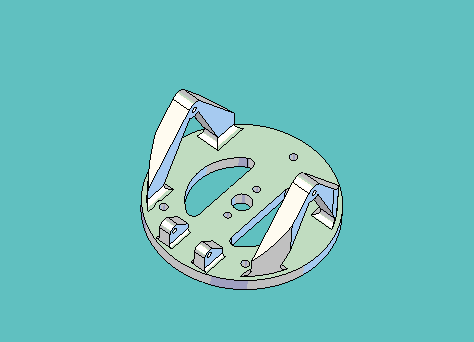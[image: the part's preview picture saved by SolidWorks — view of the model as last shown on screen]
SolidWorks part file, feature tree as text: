
SOLIDWORKS PART (.sldprt)
format: sldprt  version: not decoded by parser v0  size: 1,202,688 bytes
history: native  units: mm
features: sketch x15, cut_extrude x10, plane x7, extrude x5, fillet x3, material x1 (+11 scaffold rows collapsed)
feature tree (52):
  scaffold x11  (default folders/planes/origin — collapsed)
  material  "Material <not specified>"
  sketch  "Sketch1"  dims[c1.D1=50.8mm c1.D7=3.175mm c2.D1=89.1032mm c2.D2=~93.32036mm c3.D2=45.0deg c3.D3=~94.913632mm c4.D3=45.0deg c4.D4=6.35mm c4.D5=6.35mm c4.D6=31.75mm]
  extrude  "Extrude1"  Depth=6.35mm
  sketch  "Sketch2"  dims[c1.D1=50.8mm c1.D7=~3.96875mm c2.D1=~3.96875mm c2.D4=~3.96875mm c2.D6=69.85mm c2.D2=~93.32036mm c3.D2=163.0deg c3.D3=~94.913632mm c4.D3=45.0deg c4.D4=4.7625mm c4.D5=4.7625mm c4.D6=31.75mm c4.D1=4.7625mm c5.D6=34.925mm c5.D2=~82.034109mm c6.D2=30.0deg c6.D3=~82.034109mm c7.D3=107.0deg c7.D5=~82.034109mm c8.D5=167.0deg]
  cut_extrude  "Cut-Extrude8"  [1 undecoded]
  sketch  "Sketch3"  dims[c1.D1=3.4544mm c1.D2=3.4544mm c1.D3=9.525mm c1.D5=~19.84375mm c1.D4=~65.353861mm c2.D4=30.0deg]
  cut_extrude  "Cut-Extrude2"  [1 undecoded]
  sketch  "Sketch5"  dims[c1.D3=19.05mm c1.D4=25.4mm c1.D1=20.6375mm c1.D2=20.6375mm c1.D5=~49.79749mm c2.D5=30.0deg c2.D6=11.1125mm c2.D1=17.145mm c2.D2=17.145mm c3.D1=~82.457251mm c4.D1=90.0deg c4.D2=9.525mm c4.D3=9.525mm]
  cut_extrude  "Cut-Extrude4"  [1 undecoded]
  fillet  "Fillet2"  Radius=3.175mm
  sketch  "Sketch6"  dims[D1=9.525mm]
  extrude  "Axis2"  [1 undecoded]
  plane  "Plane1"
  plane  "Plane2"
  plane  "Plane3"  Offset=50.8mm
  sketch  "Sketch11"  dims[c1.D1=40.3225mm c1.D2=40.3225mm c2.D1=22.86mm c2.D2=24.384mm c2.D3=30.1625mm c2.D4=30.1625mm]
  extrude  "Extrude6"  Depth=44.45mm
  sketch  "Sketch7"  dims[D1=2.7051mm D2=4.7625mm]
  cut_extrude  "Cut-Extrude7"  [1 undecoded]
  sketch  "Sketch12"  dims[D1=6.35mm D2=6.35mm D3=6.35mm]
  cut_extrude  "Cut-Extrude9"  [1 undecoded]
  sketch  "Sketch15"  dims[c1.D4=3.175mm c1.D1=9.525mm c1.D2=9.525mm c1.D3=9.525mm c2.D1=9.525mm c2.D2=9.525mm c2.D5=25.4mm c2.D6=25.4mm]
  cut_extrude  "Cut-Extrude12"  [1 undecoded]
  fillet  "Fillet3"  Radius=3.175mm
  sketch  "Sketch16"  dims[D1=7.9375mm D2=7.9375mm]
  cut_extrude  "Cut-Extrude13"  [1 undecoded]
  plane  "Plane4"  Offset=7.14375mm
  plane  "Plane5"  Offset=7.14375mm
  sketch  "Sketch17"  dims[c1.D4=2.7051mm c1.D1=28.575mm c1.D2=9.525mm c1.D3=6.35mm c2.D1=38.1mm c2.D5=~9.745748mm c2.D3=9.525mm c3.D5=6.35mm c3.D6=3.175mm c3.D2=~11.90625mm c4.D5=~8.73125mm c4.D7=4.7625mm]
  extrude  "Extrude8"  Depth=5.969mm
  sketch  "Sketch18"  dims[D1=0.0mm]
  extrude  "Extrude9"  Depth=5.969mm
  fillet  "Fillet5"  Radius=1.5875mm
  plane  "Plane6"  Offset=39.6875mm
  plane  "Plane7"  Offset=39.6875mm
  sketch  "Sketch19"  dims[D1=12.7mm]
  cut_extrude  "Cut-Extrude14"  [1 undecoded]
  sketch  "Sketch20"
  cut_extrude  "Cut-Extrude15"  [1 undecoded]
  sketch  "Sketch21"  dims[D1=~2.38125mm]
  cut_extrude  "Cut-Extrude16"  [1 undecoded]
decode coverage: 21 of 33 modeling features carry decoded parameters
note: ~ marks probable driven/reference dimensions
note: 11 parameter values undecoded
summary: no parameter record found for 11 features
note: suppression state not decoded; provenance and decode notes live in map.json
